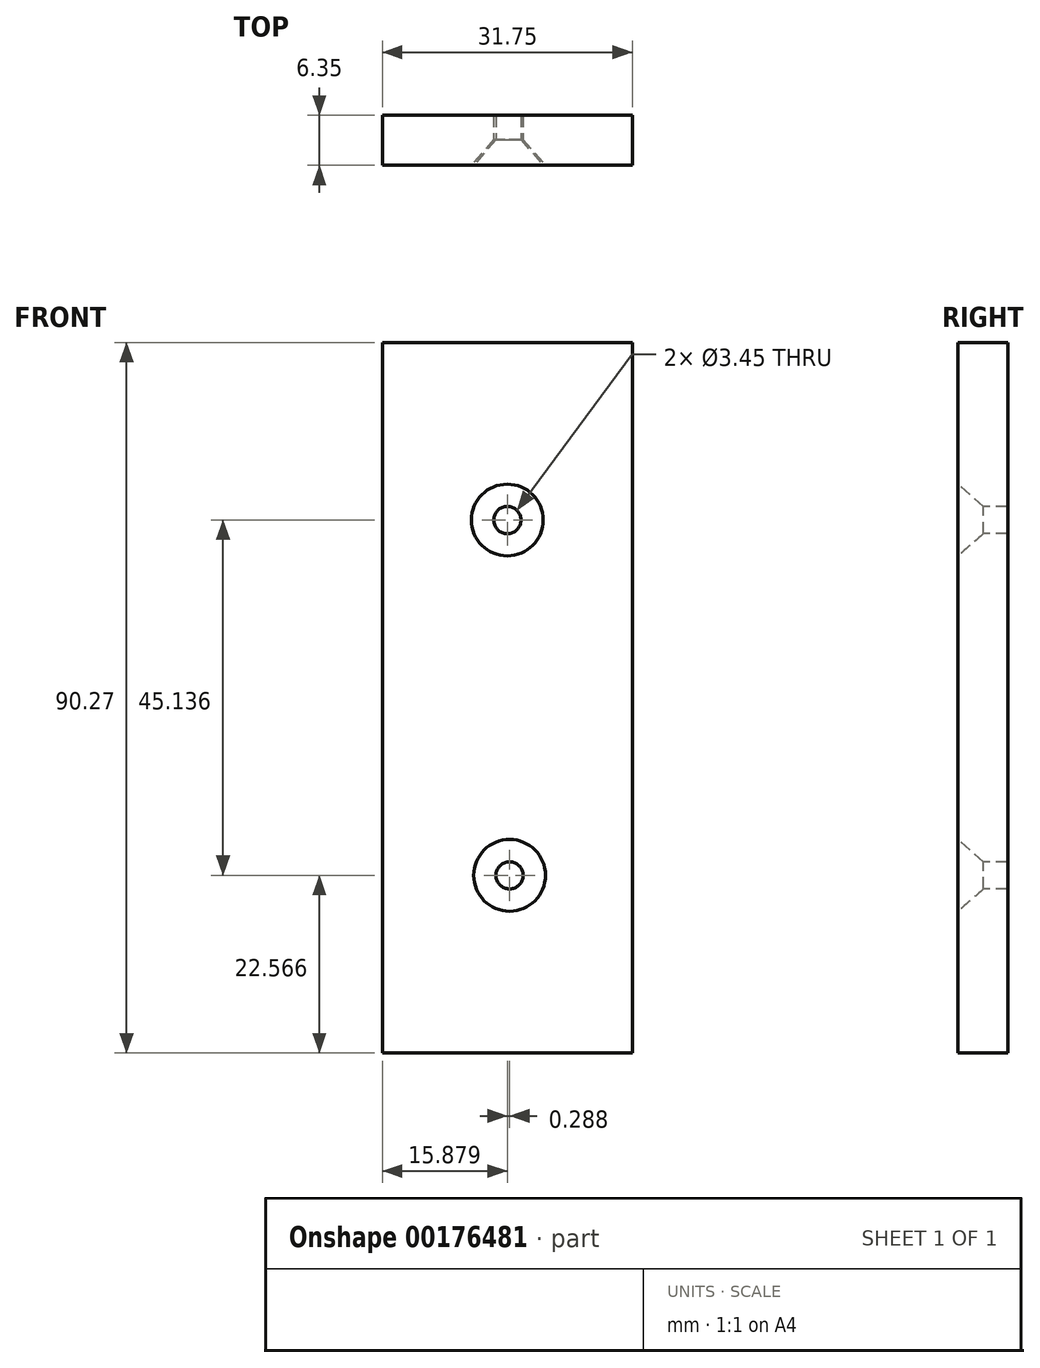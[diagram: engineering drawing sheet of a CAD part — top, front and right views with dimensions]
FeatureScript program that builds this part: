
annotation { "Feature Type Name" : "Feature", "Feature Type Description" : "" }
export const myFeature = defineFeature(function(context is Context, id is Id, definition is map)
    precondition{}
    {
        {
            var Q0;
            Q0=qCreatedBy(makeId("Front.planeOp"),FACE);
            var sketch = newSketch(context, id + "F0", { "sketchPlane" : qUnion([Q0])});
            skLineSegment(sketch, "E0.bottom", {"start": v(-20.03, -20.56) * mm, "end": v(11.72, -20.56) * mm});
            skLineSegment(sketch, "E0.top", {"start": v(-20.03, 69.7) * mm, "end": v(11.72, 69.7) * mm});
            skLineSegment(sketch, "E0.left", {"start": v(-20.03, -20.56) * mm, "end": v(-20.03, 69.7) * mm});
            skLineSegment(sketch, "E0.right", {"start": v(11.72, -20.56) * mm, "end": v(11.72, 69.7) * mm});
            skPoint(sketch, "E1", {"position": v(-4.15, 47.14) * mm});
            skPoint(sketch, "E2.MirrorP", {"position": v(-4.15, 2) * mm});
            skSolve(sketch);
        }
        {
            var Q0;
            Q0=makeQuery(id+"F0.imprint","IMPRINT",FACE,{"disambiguationData":[TD([[makeQuery(id+"F0.imprint","IMPRINT",EDGE,{"derivedFrom":sQuery(id+"F0.wireOp",EDGE,"E0.bottom")}),1.0]])]});
            var Q1;
            Q1=sQuery(id+"F0.wireOp",EDGE,"E0.left");
            var Q2;
            Q2=sQuery(id+"F0.wireOp",EDGE,"E0.right");
            var Q3;
            Q3=sQuery(id+"F0.wireOp",EDGE,"E0.top");
            var Q4;
            Q4=sQuery(id+"F0.wireOp",EDGE,"E0.bottom");
            extrude(context, id + "F1", {"entities" : qUnion([Q0]), "surfaceEntities" : qUnion([Q1, Q2, Q3, Q4]), "depth" : 6.35 * mm});
        }
        {
            var Q0;
            Q0=makeQuery(id+"F1.opExtrude","CAP_FACE",FACE,{"disambiguationData":[OSD([sQuery(id+"F0.wireOp",EDGE,"E0.bottom"),sQuery(id+"F0.wireOp",EDGE,"E0.top"),sQuery(id+"F0.wireOp",EDGE,"E0.left"),sQuery(id+"F0.wireOp",EDGE,"E0.right")])],"isStart":false});
            var sketch = newSketch(context, id + "F2", { "sketchPlane" : qUnion([Q0])});
            skPoint(sketch, "E3", {"position": v(-4.15, 47.14) * mm});
            skPoint(sketch, "E4", {"position": v(-3.86, 2) * mm});
            skSolve(sketch);
        }
        {
            var Q0;
            Q0=sQuery(id+"F2.wireOp",VERTEX,"E3");
            var Q1;
            Q1=sQuery(id+"F2.wireOp",VERTEX,"E4");
            var Q2;
            Q2=makeQuery(id+"F1.opExtrude","SWEPT_BODY",BODY,{"disambiguationData":[OSD([sQuery(id+"F0.wireOp",EDGE,"E0.bottom"),sQuery(id+"F0.wireOp",EDGE,"E0.top"),sQuery(id+"F0.wireOp",EDGE,"E0.left"),sQuery(id+"F0.wireOp",EDGE,"E0.right")])]});
            hole(context, id + "F3", {"style" : HoleStyle.C_SINK, "endStyle" : HoleEndStyle.THROUGH, "standardTappedOrClearance" : lookupTablePath({ "standard" : "ANSI", "engagement" : "75%", "pitch" : "32 tpi", "size" : "#8", "type" : "Tapped" }), "standardBlindInLast" : lookupTablePath({ "standard" : "ANSI", "engagement" : "75%", "pitch" : "32 tpi", "size" : "#8", "type" : "Tapped" }), "holeDiameter" : 3.45 * mm, "cSinkDiameter" : 9.12 * mm, "cSinkAngle" : 82 * degree, "startFromSketch" : true, "locations" : qUnion([Q0, Q1]), "scope" : qUnion([Q2]), "isTappedThrough" : true, "majorDiameter" : 4.17 * mm, "showTappedDepth" : true});
        }
    });
